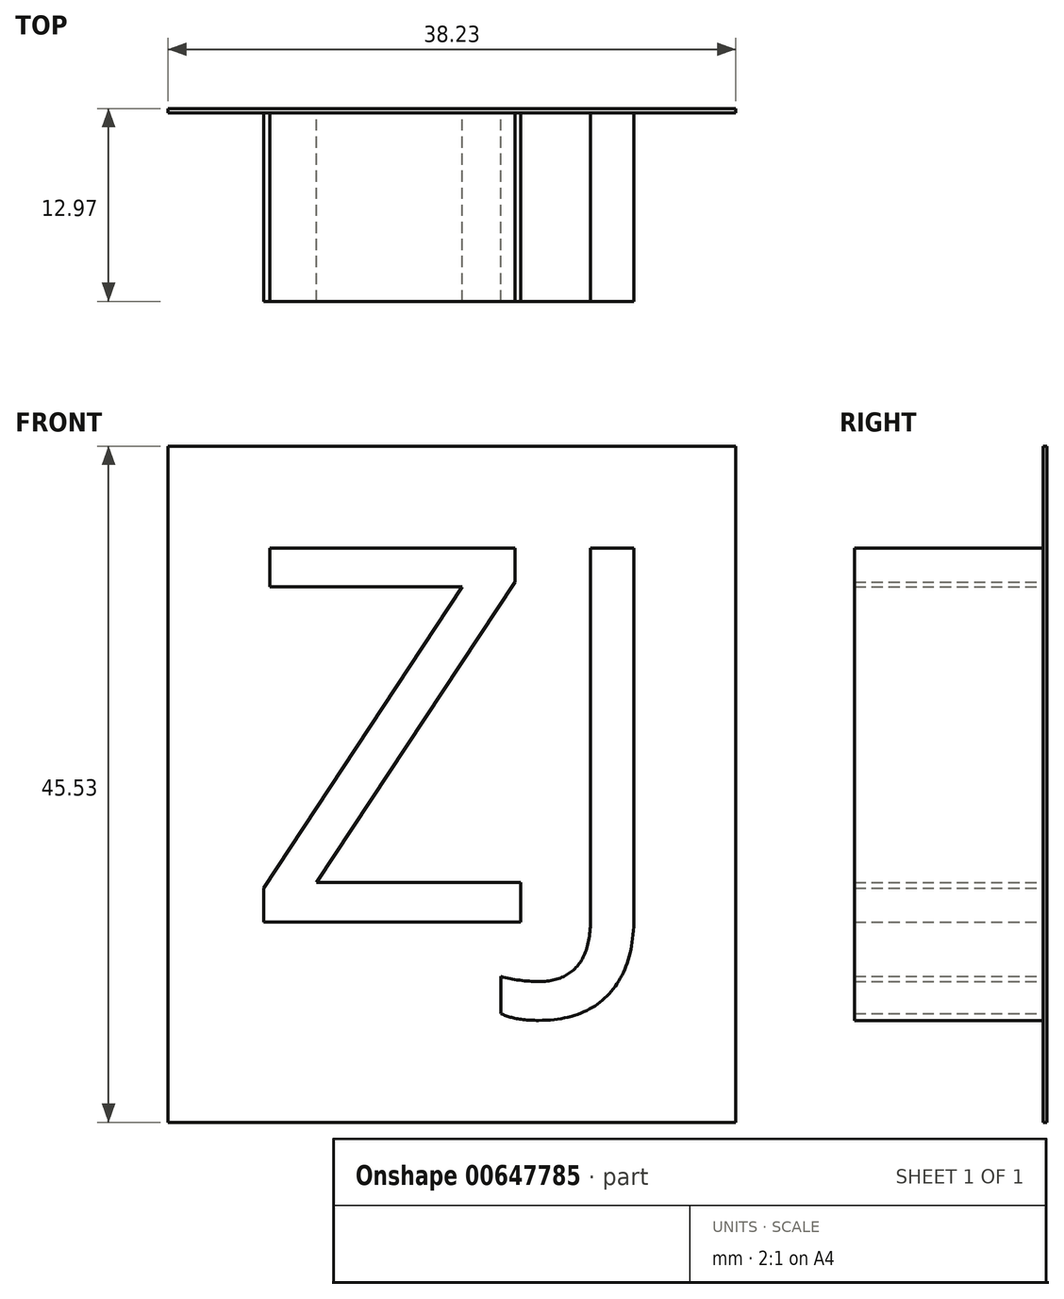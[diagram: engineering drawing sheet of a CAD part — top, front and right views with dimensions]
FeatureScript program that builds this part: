
annotation { "Feature Type Name" : "Feature", "Feature Type Description" : "" }
export const myFeature = defineFeature(function(context is Context, id is Id, definition is map)
    precondition{}
    {
        {
            assignVariable(context, id + "F0", {"name" : "spacing", "anyValue" : .27});
        }
        {
            var Q0;
            Q0=qCreatedBy(makeId("Front.planeOp"),FACE);
            var sketch = newSketch(context, id + "F1", { "sketchPlane" : qUnion([Q0])});
            skText(sketch, "E0", { "text": "ZJ", "fontName": "OpenSans-Regular.ttf"});
            const initialGuessF1  = {"E0": [-0.01547, -0.01373, 1, 0, 0.0254]};
            skSetInitialGuess(sketch, initialGuessF1);
            skSolve(sketch);
        }
        {
            var Q0;
            Q0 = qSketchRegion(id + "F1", true);
            extrude(context, id + "F2", {"entities" : qUnion([Q0]), "depth" : 12.7 * mm, "offsetDistance" : 25.4 * mm});
        }
        {
            var Q0;
            Q0=makeQuery(id+"F2.opExtrude","CAP_FACE",FACE,{"disambiguationData":[OSD([sQuery(id+"F1.wireOp",EDGE,"E0.sketch_text.stroke-0"),sQuery(id+"F1.wireOp",EDGE,"E0.sketch_text.stroke-1"),sQuery(id+"F1.wireOp",EDGE,"E0.sketch_text.stroke-2"),sQuery(id+"F1.wireOp",EDGE,"E0.sketch_text.stroke-3"),sQuery(id+"F1.wireOp",EDGE,"E0.sketch_text.stroke-4"),sQuery(id+"F1.wireOp",EDGE,"E0.sketch_text.stroke-5"),sQuery(id+"F1.wireOp",EDGE,"E0.sketch_text.stroke-6"),sQuery(id+"F1.wireOp",EDGE,"E0.sketch_text.stroke-7"),sQuery(id+"F1.wireOp",EDGE,"E0.sketch_text.stroke-8"),sQuery(id+"F1.wireOp",EDGE,"E0.sketch_text.stroke-9")])],"isStart":false});
            var sketch = newSketch(context, id + "F3", { "sketchPlane" : qUnion([Q0])});
            skLineSegment(sketch, "E1.bottom", {"start": v(3.26, -11.08) * mm, "end": v(7.94, -11.08) * mm});
            skLineSegment(sketch, "E1.top", {"start": v(3.26, -13.73) * mm, "end": v(7.94, -13.73) * mm});
            skLineSegment(sketch, "E1.left", {"start": v(3.26, -11.08) * mm, "end": v(3.26, -13.73) * mm});
            skLineSegment(sketch, "E1.right", {"start": v(7.94, -11.08) * mm, "end": v(7.94, -13.73) * mm});
            skSolve(sketch);
        }
        {
            var Q0;
            Q0=qCreatedBy(makeId("Front.planeOp"),FACE);
            var sketch = newSketch(context, id + "F4", { "sketchPlane" : qUnion([Q0])});
            skLineSegment(sketch, "E2.bottom", {"start": v(-20.5, 18.3) * mm, "end": v(17.73, 18.3) * mm});
            skLineSegment(sketch, "E2.top", {"start": v(-20.5, -27.22) * mm, "end": v(17.73, -27.22) * mm});
            skLineSegment(sketch, "E2.left", {"start": v(-20.5, 18.3) * mm, "end": v(-20.5, -27.22) * mm});
            skLineSegment(sketch, "E2.right", {"start": v(17.73, 18.3) * mm, "end": v(17.73, -27.22) * mm});
            skSolve(sketch);
        }
        {
            var Q0;
            Q0 = qSketchRegion(id + "F4", true);
            extrude(context, id + "F5", {"entities" : qUnion([Q0]), "operationType" : NewBodyOperationType.ADD, "oppositeDirection" : true, "depth" : (getVariable(context, 'spacing')) * mm, "offsetDistance" : 25.4 * mm});
        }
    });
